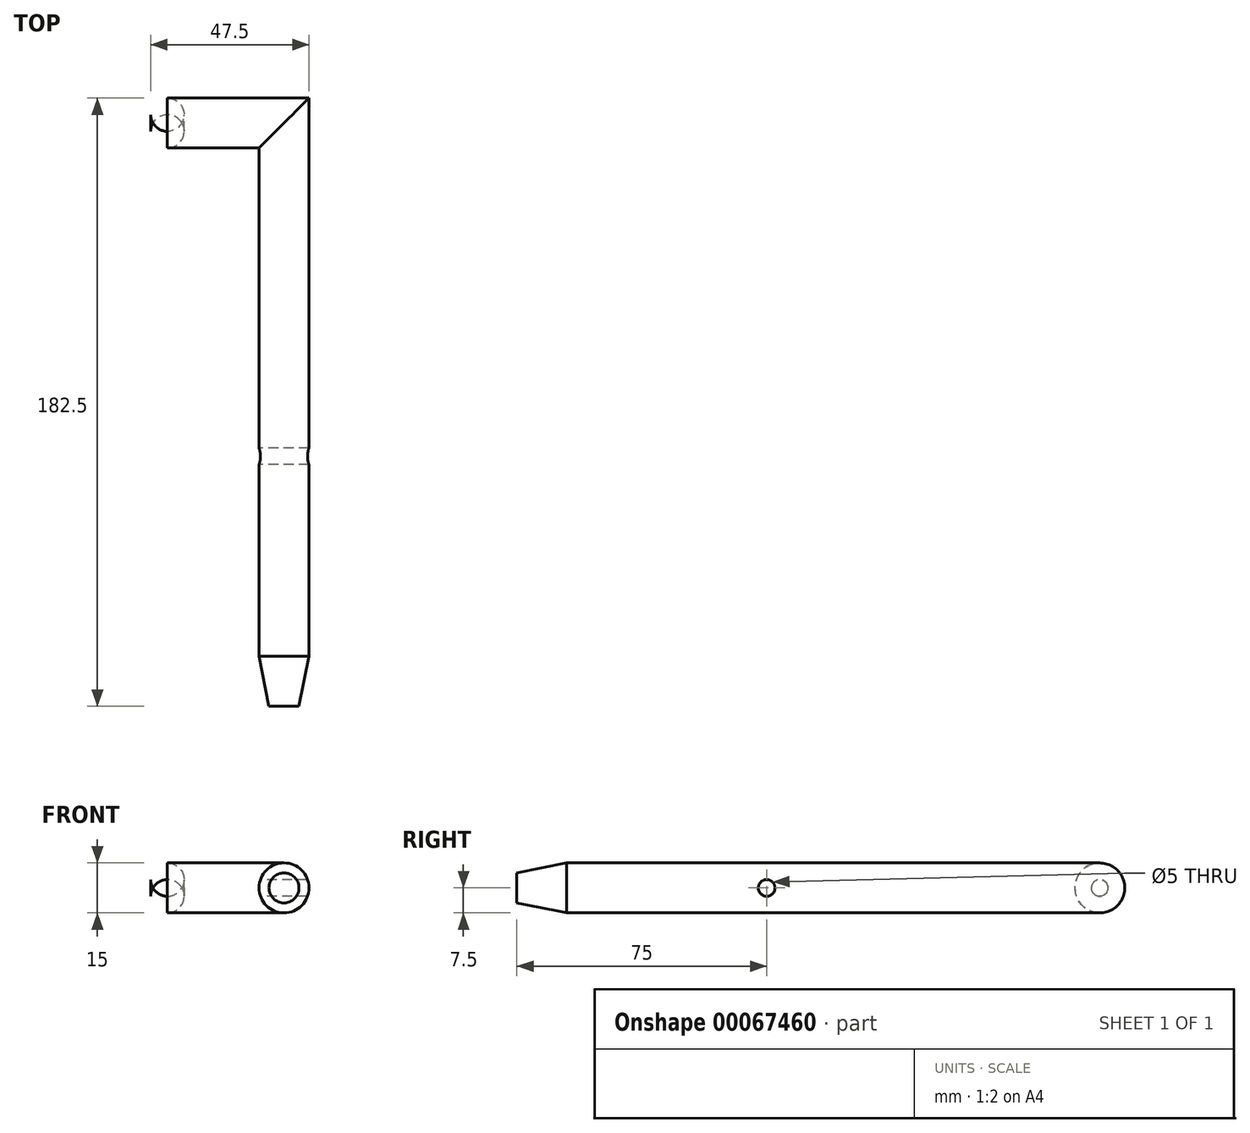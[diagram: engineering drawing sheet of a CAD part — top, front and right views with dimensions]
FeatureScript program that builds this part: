
annotation { "Feature Type Name" : "Feature", "Feature Type Description" : "" }
export const myFeature = defineFeature(function(context is Context, id is Id, definition is map)
    precondition{}
    {
        {
            var Q0;
            Q0=qCreatedBy(makeId("Front.planeOp"),FACE);
            var sketch = newSketch(context, id + "F0", { "sketchPlane" : qUnion([Q0])});
            skCircle(sketch, "E0", {"center": v(0, 0) * mm, "radius": 7.5 * mm});
            skSolve(sketch);
        }
        {
            var Q0;
            Q0 = qSketchRegion(id + "F0", true);
            extrude(context, id + "F1", {"entities" : qUnion([Q0]), "depth" : 75 * mm});
        }
        {
            var Q0;
            Q0=qCreatedBy(makeId("Top.planeOp"),FACE);
            var sketch = newSketch(context, id + "F2", { "sketchPlane" : qUnion([Q0])});
            skLineSegment(sketch, "E1", {"start": v(0, 0) * mm, "end": v(0, 100) * mm});
            skLineSegment(sketch, "E2", {"start": v(0, 100) * mm, "end": v(-40, 100) * mm});
            skSolve(sketch);
        }
        {
            var Q0;
            Q0=makeQuery(id+"F1.opExtrude","CAP_FACE",FACE,{"disambiguationData":[OSD([sQuery(id+"F0.wireOp",EDGE,"E0")])],"isStart":true});
            var Q1;
            Q1 = qConstructionFilter(qBodyType(qCreatedBy(id + "F2" ,EDGE), BodyType.WIRE), ConstructionObject.NO);
            sweep(context, id + "F3", {"operationType" : NewBodyOperationType.ADD, "profiles" : qUnion([Q0]), "path" : qUnion([Q1])});
        }
        {
            var Q0;
            Q0=qCreatedBy(makeId("Right.planeOp"),FACE);
            var sketch = newSketch(context, id + "F4", { "sketchPlane" : qUnion([Q0])});
            skPoint(sketch, "E3", {"position": v(0, 0) * mm});
            skCircle(sketch, "E4", {"center": v(0, 0) * mm, "radius": 2.5 * mm});
            skSolve(sketch);
        }
        {
            var Q0;
            Q0 = qSketchRegion(id + "F4", true);
            extrude(context, id + "F5", {"entities" : qUnion([Q0]), "operationType" : NewBodyOperationType.ADD, "endBound" : BoundingType.SYMMETRIC, "depth" : 15 * mm});
        }
        {
            var Q0;
            Q0=makeQuery(id+"F5.opExtrude","CAP_FACE",FACE,{"disambiguationData":[OSD([sQuery(id+"F4.wireOp",EDGE,"E4")])],"isStart":true});
            var sketch = newSketch(context, id + "F6", { "sketchPlane" : qUnion([Q0])});
            skPoint(sketch, "E5", {"position": v(0, 0) * mm});
            skSolve(sketch);
        }
        {
            var Q0;
            Q0=sQuery(id+"F6.wireOp",VERTEX,"E5");
            var Q1;
            Q1=makeQuery(id+"F1.opExtrude","SWEPT_BODY",BODY,{"disambiguationData":[OSD([sQuery(id+"F0.wireOp",EDGE,"E0")])]});
            hole(context, id + "F7", {"style" : HoleStyle.SIMPLE, "holeDiameter" : 5 * mm, "endStyle" : HoleEndStyle.THROUGH, "locations" : qUnion([Q0]), "scope" : qUnion([Q1])});
        }
        {
            var Q0;
            Q0=makeQuery(id+"F1.opExtrude","CAP_EDGE",EDGE,{"disambiguationData":[OSD([sQuery(id+"F0.wireOp",EDGE,"E0")])],"isStart":false});
            chamfer(context, id + "F8", {"entities" : qUnion([Q0]), "chamferType" : ChamferType.TWO_OFFSETS, "width1" : 15 * mm, "oppositeDirection" : true, "width2" : 3 * mm, "tangentPropagation" : true});
        }
        {
            var Q0;
            Q0=makeQuery(id+"F3.opSweep","CAP_EDGE",EDGE,{"disambiguationData":[OSD([sQuery(id+"F0.wireOp",EDGE,"E0"),sQuery(id+"F2.wireOp",VERTEX,"E2.end")])],"isStart":false});
            fillet(context, id + "F9", {"entities" : qUnion([Q0]), "radius" : 5 * mm, "tangentPropagation" : true, "allowEdgeOverflow" : false});
        }
    });
